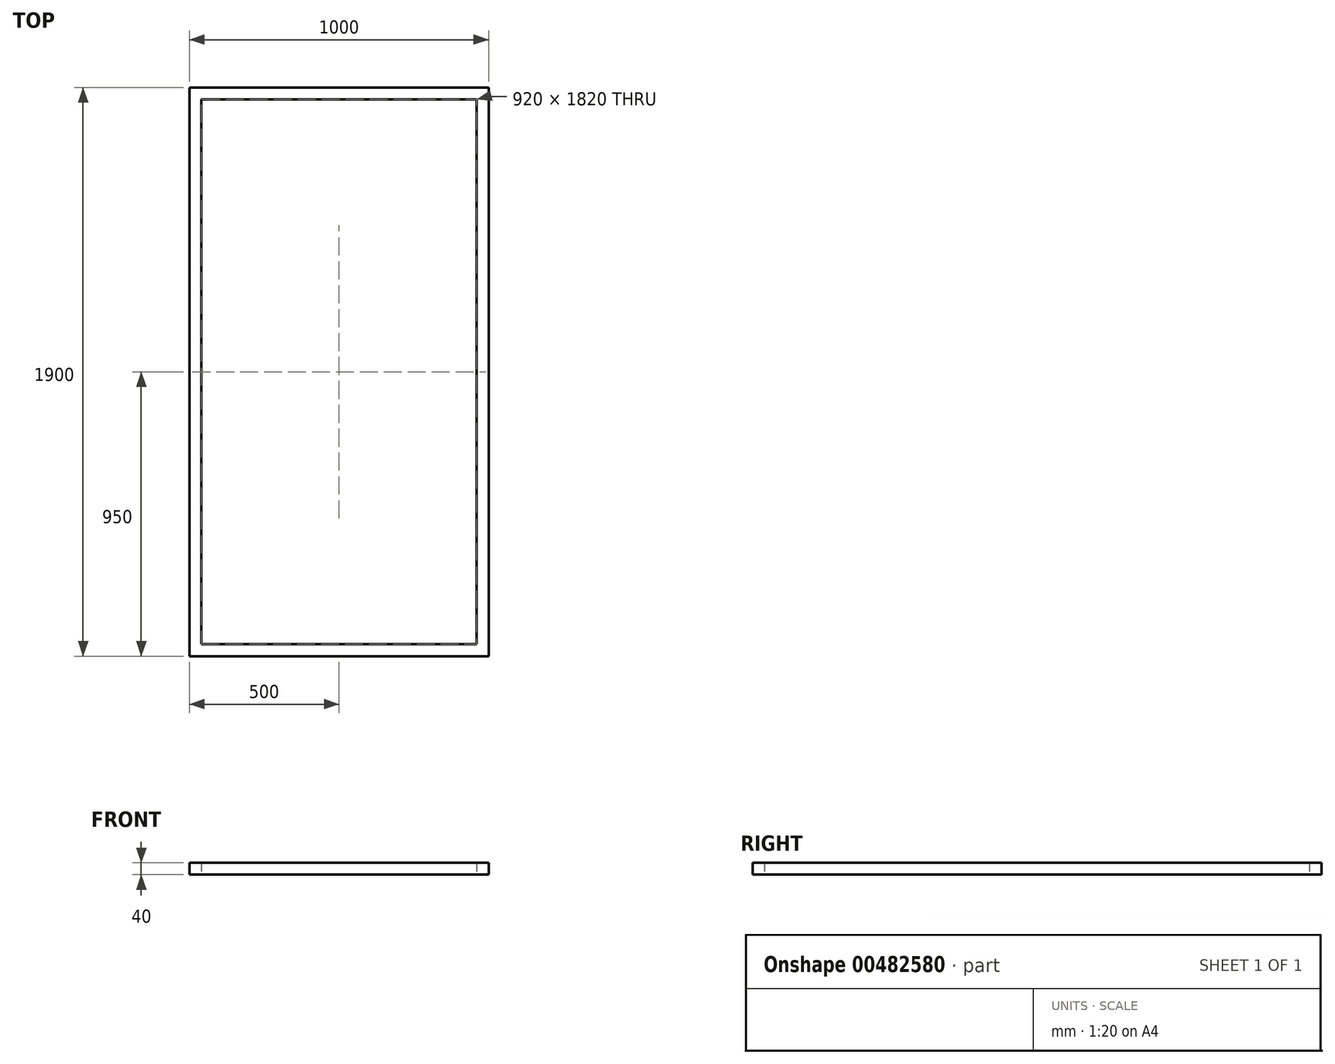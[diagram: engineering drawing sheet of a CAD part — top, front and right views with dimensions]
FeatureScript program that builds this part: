
annotation { "Feature Type Name" : "Feature", "Feature Type Description" : "" }
export const myFeature = defineFeature(function(context is Context, id is Id, definition is map)
    precondition{}
    {
        {
            var Q0;
            Q0=qCreatedBy(makeId("Top.planeOp"), FACE);
            var sketch = newSketch(context, id + "F0", { "sketchPlane" : qUnion([Q0])});
            skLineSegment(sketch, "E0.bottom", {"start": v(500, -950) * mm, "end": v(-500, -950) * mm});
            skLineSegment(sketch, "E0.top", {"start": v(500, 950) * mm, "end": v(-500, 950) * mm});
            skLineSegment(sketch, "E0.left", {"start": v(500, -950) * mm, "end": v(500, 950) * mm});
            skLineSegment(sketch, "E0.right", {"start": v(-500, -950) * mm, "end": v(-500, 950) * mm});
            skPoint(sketch, "E0.middle", {"position": v(0, 0) * mm});
            skLineSegment(sketch, "E1.0", {"start": v(-460, -910) * mm, "end": v(-460, 910) * mm});
            skLineSegment(sketch, "E1.1", {"start": v(460, 910) * mm, "end": v(-460, 910) * mm});
            skLineSegment(sketch, "E1.2", {"start": v(460, -910) * mm, "end": v(460, 910) * mm});
            skLineSegment(sketch, "E1.3", {"start": v(460, -910) * mm, "end": v(-460, -910) * mm});
            skSolve(sketch);
        }
        {
            var Q0;
            Q0 = qSketchRegion(id + "F0", true);
            extrude(context, id + "F1", {"entities" : qUnion([Q0]), "depth" : 40 * mm, "offsetDistance" : 25 * mm});
        }
    });
